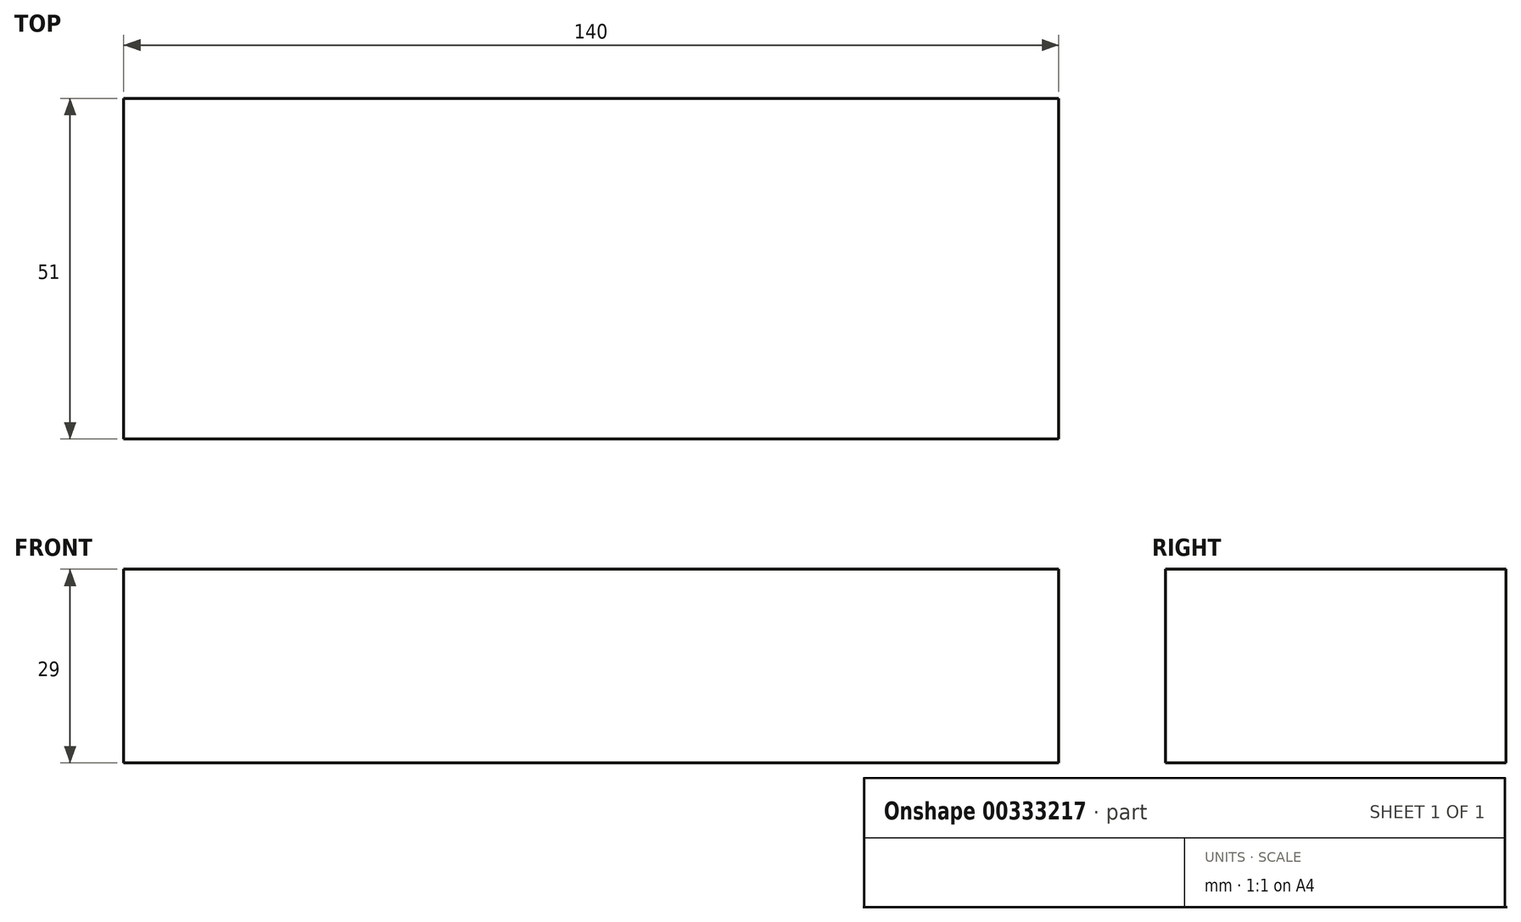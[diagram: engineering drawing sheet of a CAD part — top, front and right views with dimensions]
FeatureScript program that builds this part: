
annotation { "Feature Type Name" : "Feature", "Feature Type Description" : "" }
export const myFeature = defineFeature(function(context is Context, id is Id, definition is map)
    precondition{}
    {
        {
            var Q0;
            Q0=qCreatedBy(makeId("Top.planeOp"),FACE);
            var sketch = newSketch(context, id + "F0", { "sketchPlane" : qUnion([Q0])});
            skLineSegment(sketch, "E0.bottom", {"start": v(70, -25.5) * mm, "end": v(-70, -25.5) * mm});
            skLineSegment(sketch, "E0.top", {"start": v(70, 25.5) * mm, "end": v(-70, 25.5) * mm});
            skLineSegment(sketch, "E0.left", {"start": v(70, -25.5) * mm, "end": v(70, 25.5) * mm});
            skLineSegment(sketch, "E0.right", {"start": v(-70, -25.5) * mm, "end": v(-70, 25.5) * mm});
            skPoint(sketch, "E0.middle", {"position": v(0, 0) * mm});
            skSolve(sketch);
        }
        {
            var Q0;
            Q0=qSketchRegion(id+"F0",true);
            extrude(context, id + "F1", {"entities" : qUnion([Q0]), "depth" : 29 * mm});
        }
    });
